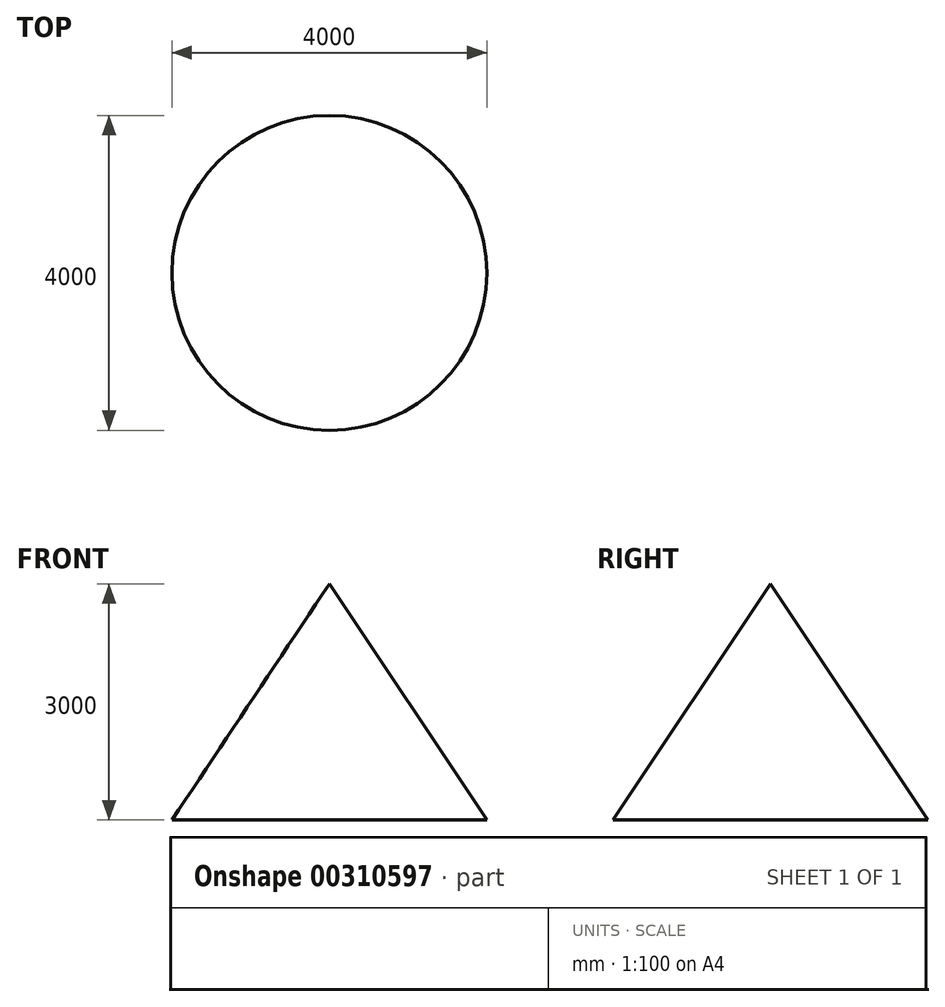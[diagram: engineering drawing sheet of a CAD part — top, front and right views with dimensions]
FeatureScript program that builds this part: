
annotation { "Feature Type Name" : "Feature", "Feature Type Description" : "" }
export const myFeature = defineFeature(function(context is Context, id is Id, definition is map)
    precondition{}
    {
        {
            var Q0;
            Q0=qCreatedBy(makeId("Front.planeOp"),FACE);
            var sketch = newSketch(context, id + "F0", { "sketchPlane" : qUnion([Q0])});
            skLineSegment(sketch, "E0", {"start": v(0, 1476.32) * mm, "end": v(0, -1523.68) * mm, "construction": true});
            skLineSegment(sketch, "E1", {"start": v(0, -1523.68) * mm, "end": v(2000, -1523.68) * mm});
            skLineSegment(sketch, "E2", {"start": v(2000, -1523.68) * mm, "end": v(0, 1476.32) * mm});
            skSolve(sketch);
        }
        {
            var Q0;
            Q0=sQuery(id+"F0.wireOp",EDGE,"E0");
            var Q1;
            Q1=sQuery(id+"F0.wireOp",EDGE,"E2");
            var Q2;
            Q2=sQuery(id+"F0.wireOp",EDGE,"E1");
            var Q3;
            Q3=sQuery(id+"F0.wireOp",EDGE,"E0");
            revolve(context, id + "F1", {"bodyType" : ToolBodyType.SURFACE, "surfaceEntities" : qUnion([Q0, Q1, Q2]), "axis" : qUnion([Q3]), "revolveType" : RevolveType.FULL});
        }
    });
